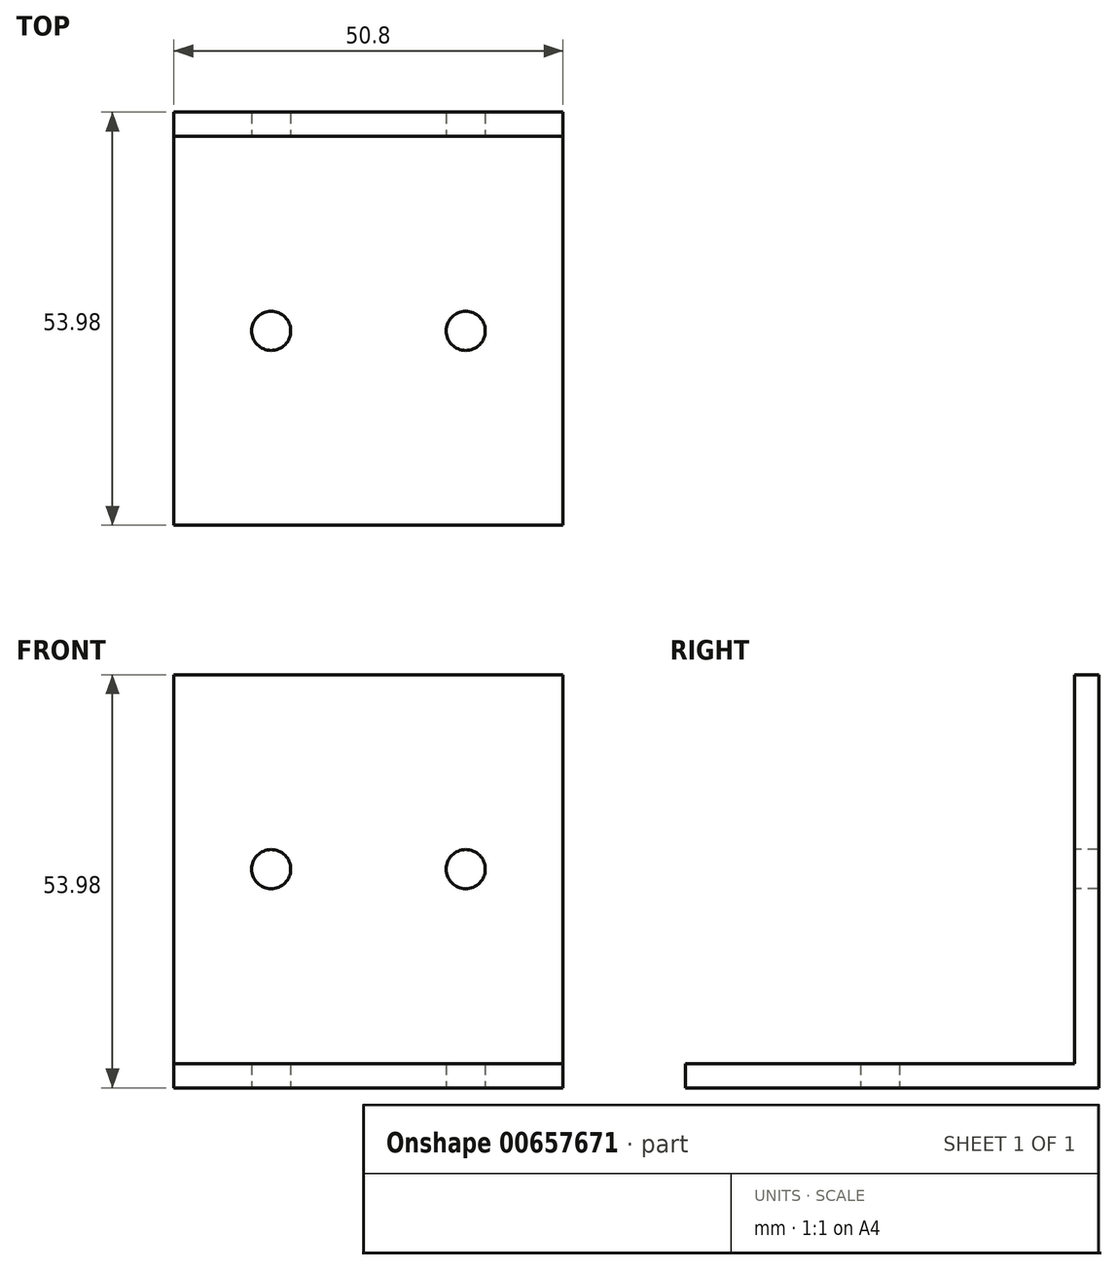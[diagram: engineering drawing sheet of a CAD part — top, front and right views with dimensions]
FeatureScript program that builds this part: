
annotation { "Feature Type Name" : "Feature", "Feature Type Description" : "" }
export const myFeature = defineFeature(function(context is Context, id is Id, definition is map)
    precondition{}
    {
        {
            var Q0;
            Q0=qCreatedBy(makeId("Top.planeOp"),FACE);
            var sketch = newSketch(context, id + "F0", { "sketchPlane" : qUnion([Q0])});
            skLineSegment(sketch, "E0.bottom", {"start": v(0, 0) * mm, "end": v(50.8, 0) * mm});
            skLineSegment(sketch, "E0.top", {"start": v(0, -53.98) * mm, "end": v(50.8, -53.98) * mm});
            skLineSegment(sketch, "E0.left", {"start": v(0, 0) * mm, "end": v(0, -53.98) * mm});
            skLineSegment(sketch, "E0.right", {"start": v(50.8, 0) * mm, "end": v(50.8, -53.98) * mm});
            skCircle(sketch, "E1", {"center": v(12.7, -28.58) * mm, "radius": 2.55 * mm});
            skCircle(sketch, "E2", {"center": v(38.1, -28.57) * mm, "radius": 2.55 * mm});
            skSolve(sketch);
        }
        {
            var Q0;
            Q0=makeQuery(id+"F0.imprint","IMPRINT",FACE,{"disambiguationData":[TD([[makeQuery(id+"F0.imprint","IMPRINT",EDGE,{"derivedFrom":sQuery(id+"F0.wireOp",EDGE,"E0.bottom")}),-1.0]])]});
            extrude(context, id + "F1", {"entities" : qUnion([Q0]), "depth" : 3.17 * mm, "offsetDistance" : 25.4 * mm});
        }
        {
            var Q0;
            Q0=makeQuery(id+"F1.opExtrude","CAP_FACE",FACE,{"disambiguationData":[OSD([sQuery(id+"F0.wireOp",EDGE,"E0.bottom"),sQuery(id+"F0.wireOp",EDGE,"E0.top"),sQuery(id+"F0.wireOp",EDGE,"E0.left"),sQuery(id+"F0.wireOp",EDGE,"E0.right"),sQuery(id+"F0.wireOp",EDGE,"E1"),sQuery(id+"F0.wireOp",EDGE,"E2")])],"isStart":false});
            var sketch = newSketch(context, id + "F2", { "sketchPlane" : qUnion([Q0])});
            skLineSegment(sketch, "E3.bottom", {"start": v(0, 0) * mm, "end": v(50.8, 0) * mm});
            skLineSegment(sketch, "E3.top", {"start": v(0, -3.18) * mm, "end": v(50.8, -3.18) * mm});
            skLineSegment(sketch, "E3.left", {"start": v(0, 0) * mm, "end": v(0, -3.18) * mm});
            skLineSegment(sketch, "E3.right", {"start": v(50.8, 0) * mm, "end": v(50.8, -3.18) * mm});
            skSolve(sketch);
        }
        {
            var Q0;
            Q0=makeQuery(id+"F2.imprint","IMPRINT",FACE,{"disambiguationData":[TD([[makeQuery(id+"F2.imprint","IMPRINT",EDGE,{"derivedFrom":sQuery(id+"F2.wireOp",EDGE,"E3.bottom")}),-1.0]])]});
            extrude(context, id + "F3", {"entities" : qUnion([Q0]), "operationType" : NewBodyOperationType.ADD, "depth" : 50.8 * mm, "offsetDistance" : 25.4 * mm});
        }
        {
            var Q0;
            Q0=makeQuery(id+"F3.opExtrude","SWEPT_FACE",FACE,{"disambiguationData":[OSD([sQuery(id+"F2.wireOp",EDGE,"E3.top")])]});
            var sketch = newSketch(context, id + "F4", { "sketchPlane" : qUnion([Q0])});
            skCircle(sketch, "E4", {"center": v(12.7, 28.57) * mm, "radius": 2.55 * mm});
            skCircle(sketch, "E5", {"center": v(38.1, 28.57) * mm, "radius": 2.55 * mm});
            skSolve(sketch);
        }
        {
            var Q0;
            Q0=makeQuery(id+"F4.imprint","IMPRINT",FACE,{"disambiguationData":[TD([[makeQuery(id+"F4.imprint","IMPRINT",EDGE,{"derivedFrom":sQuery(id+"F4.wireOp",EDGE,"E4")}),1.0]])]});
            var Q1;
            Q1=makeQuery(id+"F4.imprint","IMPRINT",FACE,{"disambiguationData":[TD([[makeQuery(id+"F4.imprint","IMPRINT",EDGE,{"derivedFrom":sQuery(id+"F4.wireOp",EDGE,"E5")}),1.0]])]});
            extrude(context, id + "F5", {"entities" : qUnion([Q0, Q1]), "operationType" : NewBodyOperationType.REMOVE, "oppositeDirection" : true, "depth" : 25.4 * mm, "offsetDistance" : 25.4 * mm});
        }
    });
